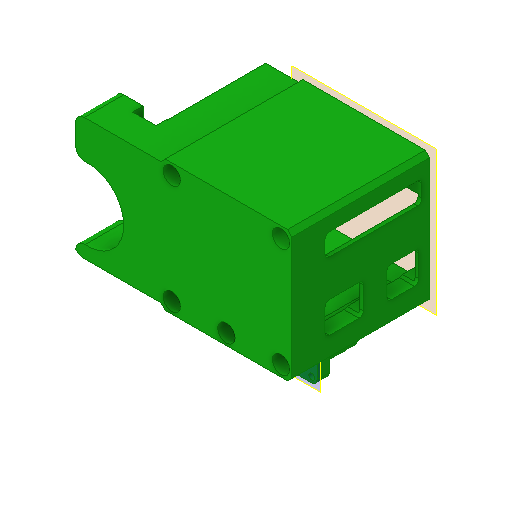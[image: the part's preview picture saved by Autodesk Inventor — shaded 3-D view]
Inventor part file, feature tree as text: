
AUTODESK INVENTOR PART (.ipt)
format: ipt  version: 2022 (Build 260153000, 153)  size: 549,888 bytes
history: native  units: mm
features: reference x22, sketch x14, other x13, extrude x10, plane x5, projected_geometry x5, hole x4, fillet x3
ambient origin geometry x8: Origin, YZ Plane, XZ Plane, XY Plane, X Axis, Y Axis, Z Axis, Center Point
bodies: Solid1 (feature_tree)
feature tree (76):
  plane  "Work Plane1"
  plane  "Arbeitsebene4"
  extrude  "Extrusion1"  Depth=10.0mm TaperAngle=0.0deg
  extrude  "Extrusion3"  Depth=5.0mm TaperAngle=0.0deg
  extrude  "Extrusion4"  Depth=10.0mm TaperAngle=0.0deg
  extrude  "Extrusion6"  Depth=4.0mm
  hole  "Hole1"  [1 undecoded]
  plane  "Arbeitsebene3"
  extrude  "Extrusion7"  Depth=3.0mm
  sketch  "Skizze12"  dims[d58=10.0mm d59=0.0mm d60=2.0mm]
  plane  "Arbeitsebene5"
  extrude  "Extrusion10"  Depth=2.0mm
  fillet  "Rundung1"  Radius=2.0mm
  hole  "Bohrung3"  [1 undecoded]
  extrude  "Extrusion12"  Depth=10.0mm TaperAngle=0.0deg
  fillet  "Rundung2"  Radius=60.0mm
  hole  "Bohrung4"  [1 undecoded]
  sketch  "Skizze17"  dims[d81=10.0mm]
  plane  "Arbeitsebene6"
  extrude  "Extrusion13"  Depth=24.0mm
  extrude  "Extrusion14"  TaperAngle=0.0deg  [1 undecoded]
  hole  "Bohrung5"  [1 undecoded]
  fillet  "Rundung3"  [1 undecoded]
  extrude  "Extrusion15"  [1 undecoded]
  sketch  "Sketch1"  dims[d0=5.0mm d1=0.0mm d7=10.0mm d8=0.0mm]
  reference  "Reference1"
  reference  "Reference2"
  reference  "Reference3"
  sketch  "Sketch3"  dims[d10=40.0mm d11=0.0mm d14=5.0mm d15=0.0mm]
  projected_geometry  "Projected Loop2"
  sketch  "Sketch4"  dims[d16=2.9mm d17=6.0mm d18=19.05mm d19=4.775mm d20=14.3117mm d21=20.0mm d22=20.594885mm d26=10.0mm d27=0.0mm]
  sketch  "Sketch6"  dims[d41=10.0mm d42=0.0mm d43=4.0mm]
  projected_geometry  "Projected Loop4"
  sketch  "Sketch7"  dims[d48=4.5mm d49=6.0mm d50=8.0mm d51=55.0mm d52=90.0deg d53=60.0mm d54=20.594885mm d55=6.0mm]
  reference  "Reference5"
  reference  "Reference6"
  reference  "Reference8"
  reference  "Reference9"
  reference  "Reference10"
  sketch  "Skizze8"  dims[d56=6.0mm d57=3.0mm]
  reference  "Referenz11"
  reference  "Referenz12"
  reference  "Referenz13"
  reference  "Referenz14"
  reference  "Referenz15"
  reference  "Referenz16"
  projected_geometry  "Projizierte Kontur9"
  reference  "Referenz18"
  sketch  "Skizze14"  dims[d61=2.8mm d62=6.0mm d63=8.0mm d64=55.0mm d65=90.0deg d66=60.0mm d67=0.0mm d68=2.0mm]
  projected_geometry  "Projizierte Kontur11"
  projected_geometry  "Projizierte Kontur12"
  sketch  "Skizze15"  dims[d69=2.0mm d70=2.0mm]
  sketch  "Skizze16"  dims[d71=2.0mm d72=10.0mm d73=0.0mm d76=60.0mm d77=0.0mm]
  reference  "Referenz20"
  reference  "Referenz21"
  reference  "Referenz22"
  reference  "Referenz23"
  sketch  "Skizze18"  dims[d82=2.8mm d83=6.0mm d84=5.0mm d85=13.0mm d86=90.0deg d87=8.0mm d88=20.594885mm d89=5.0mm]
  reference  "Referenz24"
  sketch  "Skizze19"  dims[d90=33.0mm d91=24.0mm]
  sketch  "Skizze20"  dims[d92=0.0mm d93=0.0mm d94=0.0mm]
  reference  "Referenz26"
  reference  "Referenz27"
  other  "<userpath>\Documents\GitHub\cellstorm\INVENTOR\cellSTORM_v6.iam"
  other  "cellSTORM_v6.iam"
  other  "00_XY_stage-CHUO_SEIKI_LD-647-R1:2"
  other  "00_XY_stage-CHUO_SEIKI_LD-647-R1-Bottom:1"
  other  "cellSTORM_v5_microsocpe:1"
  other  "00_NEMA11:1"
  other  "cellSTORM_v5_cellphone_craddle:1"
  other  "00_Arduino_CNC_Assembly:1"
  other  "Arduino_Uno_1"
  other  "Arduino UNO Rev.3 (CH340)-CAWEB.ORG.stp_3"
  other  "PCB.stp_4"
  other  "cellSTORM_v5_opticalstage:1"
  other  "<userpath>\Dropbox\cellSTORM\cellSTORM_v6.iam"
note: 7 required parameter values undecoded (feature->parameter linkage not recoverable at this tier; creation-order binding heuristic only, values carry confidence <= 0.55)
